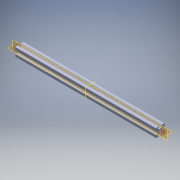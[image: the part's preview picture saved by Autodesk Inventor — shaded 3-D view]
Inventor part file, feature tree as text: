
AUTODESK INVENTOR PART (.ipt)
format: ipt  version: 2018 (Build 220112000, 112)  size: 360,960 bytes
history: native  units: in
note: dims shown in document units (in); Inventor stores cm internally (conversion verified against a paired STEP export)
features: extrude x1, plane x1, sketch x1, projected_geometry x1, fillet x1
ambient origin geometry x8: Origin, YZ Plane, XZ Plane, XY Plane, X Axis, Y Axis, Z Axis, Center Point
bodies: Solid1 (feature_tree)
feature tree (5):
  extrude  "Extrusion2"  [1 undecoded]
  plane  "Work Plane1"
  sketch  "Sketch3"  dims[d2=8.6614in d3=0.0in]
  projected_geometry  "Projected Loop2"
  fillet  "Fillet5"  [1 undecoded]
note: 2 required parameter values undecoded (feature->parameter linkage not recoverable at this tier; creation-order binding heuristic only, values carry confidence <= 0.55)
